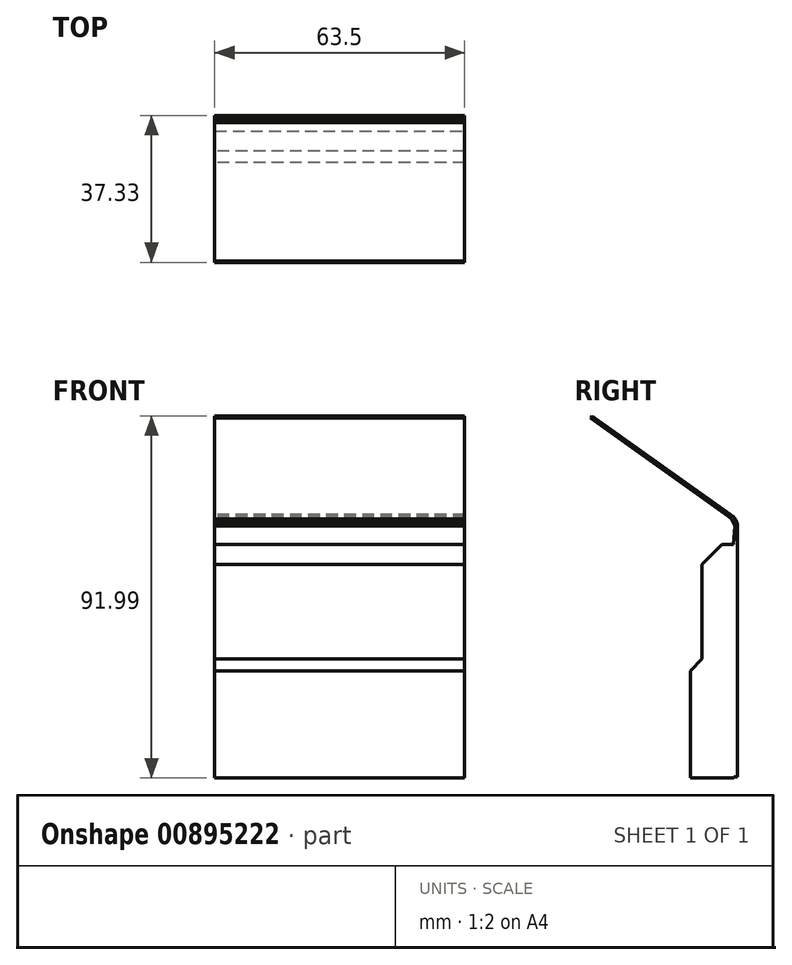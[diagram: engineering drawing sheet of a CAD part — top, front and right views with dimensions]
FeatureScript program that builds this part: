
annotation { "Feature Type Name" : "Feature", "Feature Type Description" : "" }
export const myFeature = defineFeature(function(context is Context, id is Id, definition is map)
    precondition{}
    {
        {
            var Q0;
            Q0=qCreatedBy(makeId("Right.planeOp"),FACE);
            var sketch = newSketch(context, id + "F0", { "sketchPlane" : qUnion([Q0])});
            skLineSegment(sketch, "E0.bottom", {"start": v(-5.51, 29.65) * mm, "end": v(5.51, 29.65) * mm});
            skLineSegment(sketch, "E0.top", {"start": v(-5.51, -29.65) * mm, "end": v(5.51, -29.65) * mm});
            skLineSegment(sketch, "E0.left", {"start": v(-5.51, 29.65) * mm, "end": v(-5.51, -29.65) * mm});
            skLineSegment(sketch, "E0.right", {"start": v(5.51, 29.65) * mm, "end": v(5.51, -29.65) * mm});
            skPoint(sketch, "E0.middle", {"position": v(0, 0) * mm});
            skLineSegment(sketch, "E1", {"start": v(-2.57, 29.65) * mm, "end": v(-2.57, 2.7) * mm});
            skLineSegment(sketch, "E2", {"start": v(-2.57, 2.7) * mm, "end": v(-5.51, 2.7) * mm});
            skLineSegment(sketch, "E3", {"start": v(-5.51, 2.7) * mm, "end": v(-5.51, 29.65) * mm});
            skSolve(sketch);
        }
        {
            var Q0;
            Q0=makeQuery(id+"F0.imprint","IMPRINT",FACE,{"disambiguationData":[TD([[makeQuery(id+"F0.imprint","IMPRINT",EDGE,{"derivedFrom":sQuery(id+"F0.wireOp",EDGE,"E0.top")}),1.0]])]});
            extrude(context, id + "F1", {"entities" : qUnion([Q0]), "endBound" : BoundingType.SYMMETRIC, "depth" : 63.5 * mm, "offsetDistance" : 25.4 * mm});
        }
        {
            var Q0;
            Q0=makeQuery(id+"F1.opExtrude","SWEPT_EDGE",EDGE,{"disambiguationData":[OSD([sQuery(id+"F0.wireOp",EDGE,"E0.left"),sQuery(id+"F0.wireOp",EDGE,"E2"),sQuery(id+"F0.wireOp",EDGE,"E3")])]});
            var Q1;
            Q1=makeQuery(id+"F1.opExtrude","SWEPT_EDGE",EDGE,{"disambiguationData":[OSD([sQuery(id+"F0.wireOp",EDGE,"E0.bottom"),sQuery(id+"F0.wireOp",EDGE,"E1")])]});
            chamfer(context, id + "F2", {"entities" : qUnion([Q0, Q1]), "width" : 5.08 * mm, "tangentPropagation" : true});
        }
        {
            var Q0;
            Q0=qCreatedBy(makeId("Right.planeOp"),FACE);
            var sketch = newSketch(context, id + "F3", { "sketchPlane" : qUnion([Q0])});
            skLineSegment(sketch, "E4", {"start": v(5.41, -29.4) * mm, "end": v(6.4, -29.4) * mm});
            skLineSegment(sketch, "E5", {"start": v(6.4, -29.4) * mm, "end": v(6.4, 34.82) * mm});
            skLineSegment(sketch, "E6", {"start": v(6.4, 34.82) * mm, "end": v(6.04, 35.96) * mm});
            skLineSegment(sketch, "E7", {"start": v(6.04, 35.96) * mm, "end": v(5.35, 36.77) * mm});
            skLineSegment(sketch, "E8", {"start": v(5.35, 36.77) * mm, "end": v(4.59, 37.25) * mm});
            skLineSegment(sketch, "E9", {"start": v(4.59, 37.25) * mm, "end": v(-30.5, 62.34) * mm});
            skLineSegment(sketch, "E10", {"start": v(-30.5, 62.34) * mm, "end": v(-30.92, 61.77) * mm});
            skLineSegment(sketch, "E11", {"start": v(-30.92, 61.77) * mm, "end": v(4.05, 36.77) * mm});
            skLineSegment(sketch, "E12", {"start": v(4.05, 36.77) * mm, "end": v(4.86, 36.2) * mm});
            skLineSegment(sketch, "E13", {"start": v(4.86, 36.2) * mm, "end": v(5.35, 35.33) * mm});
            skLineSegment(sketch, "E14", {"start": v(5.35, 35.33) * mm, "end": v(5.73, 34.34) * mm});
            skLineSegment(sketch, "E15", {"start": v(5.73, 34.34) * mm, "end": v(5.35, 29.56) * mm});
            skLineSegment(sketch, "E16", {"start": v(5.35, 29.56) * mm, "end": v(5.41, -29.4) * mm});
            skSolve(sketch);
        }
        {
            var Q0;
            Q0 = qSketchRegion(id + "F3", true);
            extrude(context, id + "F4", {"entities" : qUnion([Q0]), "operationType" : NewBodyOperationType.ADD, "endBound" : BoundingType.SYMMETRIC, "depth" : 63.5 * mm, "offsetDistance" : 25.4 * mm});
        }
    });
